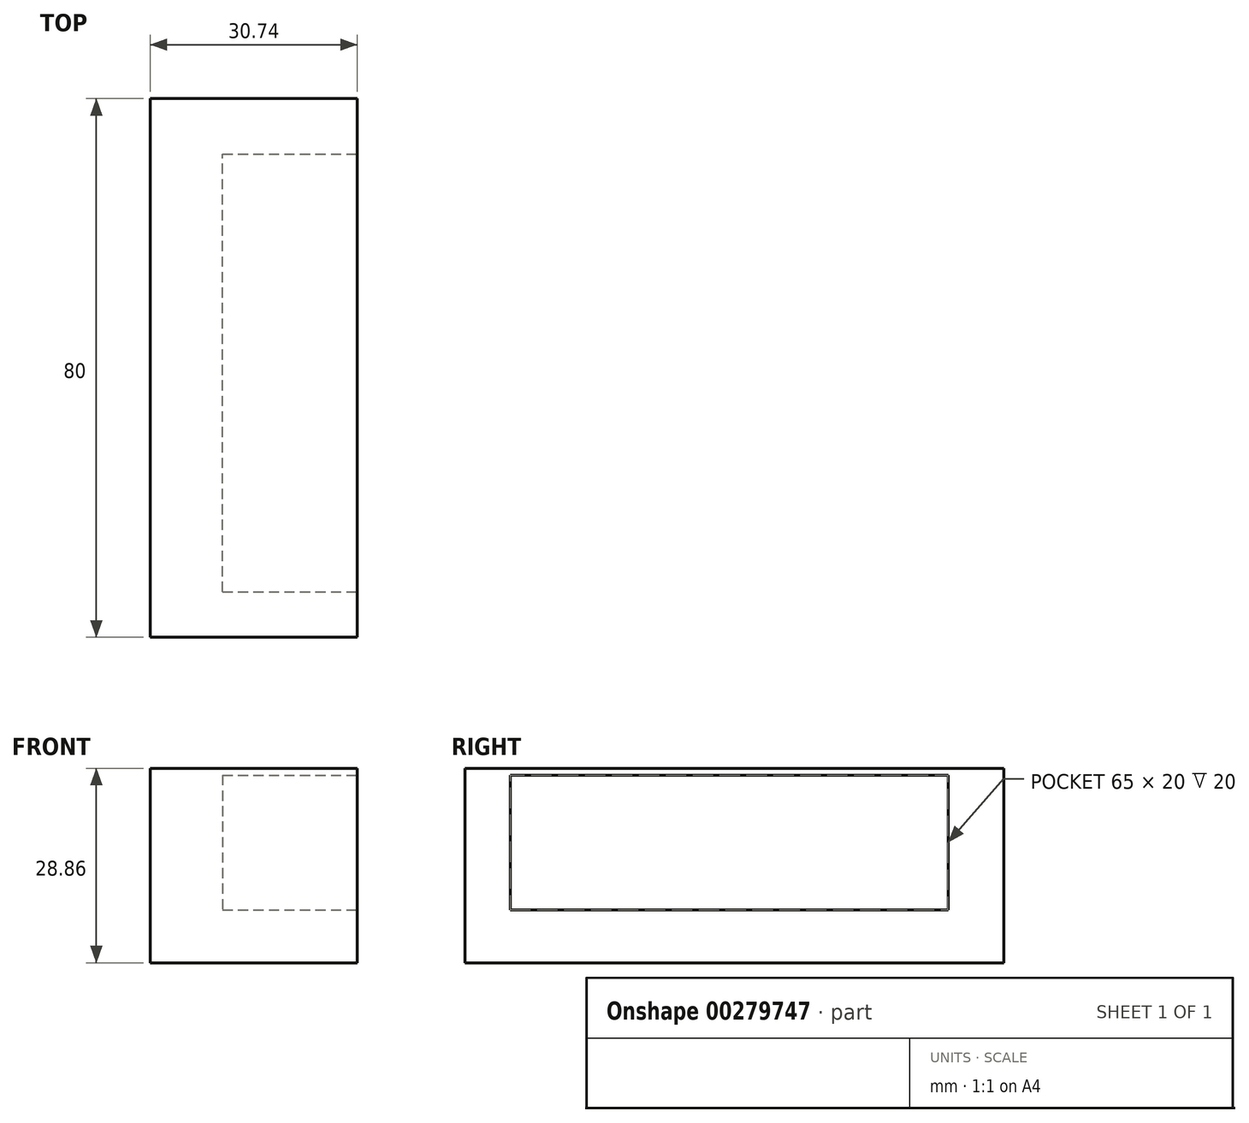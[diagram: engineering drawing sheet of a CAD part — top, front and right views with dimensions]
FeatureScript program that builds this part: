
annotation { "Feature Type Name" : "Feature", "Feature Type Description" : "" }
export const myFeature = defineFeature(function(context is Context, id is Id, definition is map)
    precondition{}
    {
        {
            var Q0;
            Q0=qCreatedBy(makeId("Front.planeOp"),FACE);
            var sketch = newSketch(context, id + "F0", { "sketchPlane" : qUnion([Q0])});
            skLineSegment(sketch, "E0.bottom", {"start": v(0, 0) * mm, "end": v(30.74, 0) * mm});
            skLineSegment(sketch, "E0.top", {"start": v(0, 28.86) * mm, "end": v(30.74, 28.86) * mm});
            skLineSegment(sketch, "E0.left", {"start": v(0, 0) * mm, "end": v(0, 28.86) * mm});
            skLineSegment(sketch, "E0.right", {"start": v(30.74, 0) * mm, "end": v(30.74, 28.86) * mm});
            skSolve(sketch);
        }
        {
            var Q0;
            Q0=makeQuery(id+"F0.imprint","IMPRINT",FACE,{"disambiguationData":[TD([[makeQuery(id+"F0.imprint","IMPRINT",EDGE,{"derivedFrom":sQuery(id+"F0.wireOp",EDGE,"E0.bottom")}),1.0]])]});
            extrude(context, id + "F1", {"entities" : qUnion([Q0]), "depth" : 80 * mm});
        }
        {
            var Q0;
            Q0=makeQuery(id+"F1.opExtrude","SWEPT_FACE",FACE,{"disambiguationData":[OSD([sQuery(id+"F0.wireOp",EDGE,"E0.right")])]});
            var sketch = newSketch(context, id + "F2", { "sketchPlane" : qUnion([Q0])});
            skLineSegment(sketch, "E1.bottom", {"start": v(-73.27, 27.87) * mm, "end": v(-8.27, 27.87) * mm});
            skLineSegment(sketch, "E1.top", {"start": v(-73.27, 7.87) * mm, "end": v(-8.27, 7.87) * mm});
            skLineSegment(sketch, "E1.left", {"start": v(-73.27, 27.87) * mm, "end": v(-73.27, 7.87) * mm});
            skLineSegment(sketch, "E1.right", {"start": v(-8.27, 27.87) * mm, "end": v(-8.27, 7.87) * mm});
            skSolve(sketch);
        }
        {
            var Q0;
            Q0 = qSketchRegion(id + "F2", true);
            extrude(context, id + "F3", {"entities" : qUnion([Q0]), "operationType" : NewBodyOperationType.REMOVE, "oppositeDirection" : true, "depth" : 20 * mm});
        }
    });
